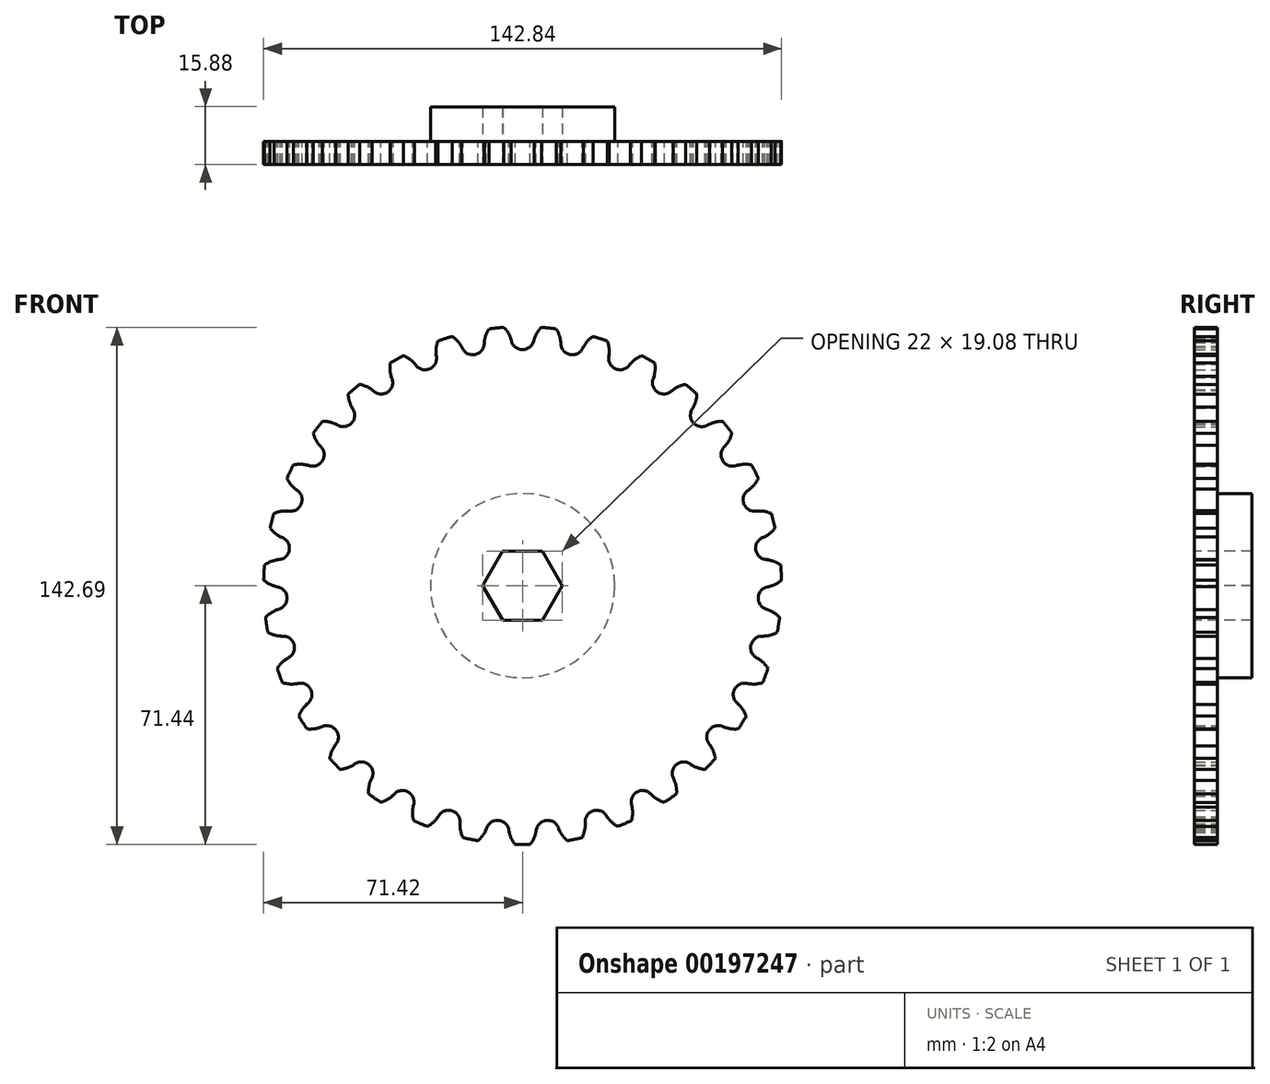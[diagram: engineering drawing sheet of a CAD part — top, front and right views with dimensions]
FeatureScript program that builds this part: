
annotation { "Feature Type Name" : "Feature", "Feature Type Description" : "" }
export const myFeature = defineFeature(function(context is Context, id is Id, definition is map)
    precondition{}
    {
        {
            var Q0;
            Q0=qCreatedBy(makeId("Front.planeOp"),FACE);
            var sketch = newSketch(context, id + "F0", { "sketchPlane" : qUnion([Q0])});
            skCircle(sketch, "E0", {"center": v(0, 0) * mm, "radius": 71.44 * mm});
            skSolve(sketch);
        }
        {
            var Q0;
            Q0 = qSketchRegion(id + "F0", true);
            extrude(context, id + "F1", {"entities" : qUnion([Q0]), "depth" : 6.35 * mm});
        }
        {
            var Q0;
            Q0=qCreatedBy(makeId("Front.planeOp"),FACE);
            var sketch = newSketch(context, id + "F2", { "sketchPlane" : qUnion([Q0])});
            skArc(sketch, "E1", {"start": v(-3.17, 68.11) * mm, "mid": v(0, 65.09) * mm, "end": v(3.17, 68.11) * mm});
            skLineSegment(sketch, "E2", {"start": v(3.17, 68.11) * mm, "end": v(3.33, 71.44) * mm});
            skLineSegment(sketch, "E3", {"start": v(-3.17, 68.11) * mm, "end": v(-3.32, 71.36) * mm});
            skPoint(sketch, "E4.start.orphan", {"position": v(0, 0) * mm});
            skArc(sketch, "E5.1.0", {"start": v(-16.82, 66.08) * mm, "mid": v(-13.1, 63.76) * mm, "end": v(-10.6, 67.36) * mm});
            skLineSegment(sketch, "E5.1.1", {"start": v(-10.6, 67.36) * mm, "end": v(-11.12, 70.64) * mm});
            skLineSegment(sketch, "E5.1.2", {"start": v(-16.82, 66.08) * mm, "end": v(-17.62, 69.23) * mm});
            skArc(sketch, "E5.2.0", {"start": v(-29.78, 61.34) * mm, "mid": v(-25.67, 59.81) * mm, "end": v(-23.95, 63.85) * mm});
            skLineSegment(sketch, "E5.2.1", {"start": v(-23.95, 63.85) * mm, "end": v(-25.12, 66.96) * mm});
            skLineSegment(sketch, "E5.2.2", {"start": v(-29.78, 61.34) * mm, "end": v(-31.2, 64.27) * mm});
            skArc(sketch, "E5.3.0", {"start": v(-41.51, 54.1) * mm, "mid": v(-37.18, 53.42) * mm, "end": v(-36.3, 57.72) * mm});
            skLineSegment(sketch, "E5.3.1", {"start": v(-36.3, 57.72) * mm, "end": v(-38.08, 60.53) * mm});
            skLineSegment(sketch, "E5.3.2", {"start": v(-41.51, 54.1) * mm, "end": v(-43.5, 56.67) * mm});
            skArc(sketch, "E5.4.0", {"start": v(-51.55, 44.63) * mm, "mid": v(-47.17, 44.84) * mm, "end": v(-47.18, 49.23) * mm});
            skLineSegment(sketch, "E5.4.1", {"start": v(-47.18, 49.23) * mm, "end": v(-49.49, 51.63) * mm});
            skLineSegment(sketch, "E5.4.2", {"start": v(-51.55, 44.63) * mm, "end": v(-54.01, 46.76) * mm});
            skArc(sketch, "E5.5.0", {"start": v(-59.48, 33.34) * mm, "mid": v(-55.24, 34.43) * mm, "end": v(-56.13, 38.72) * mm});
            skLineSegment(sketch, "E5.5.1", {"start": v(-56.13, 38.72) * mm, "end": v(-58.87, 40.61) * mm});
            skLineSegment(sketch, "E5.5.2", {"start": v(-59.48, 33.34) * mm, "end": v(-62.32, 34.93) * mm});
            skArc(sketch, "E5.6.0", {"start": v(-64.98, 20.68) * mm, "mid": v(-61.04, 22.6) * mm, "end": v(-62.77, 26.63) * mm});
            skLineSegment(sketch, "E5.6.1", {"start": v(-62.77, 26.63) * mm, "end": v(-65.84, 27.93) * mm});
            skLineSegment(sketch, "E5.6.2", {"start": v(-64.98, 20.68) * mm, "end": v(-68.07, 21.67) * mm});
            skArc(sketch, "E5.7.0", {"start": v(-67.8, 7.18) * mm, "mid": v(-64.34, 9.86) * mm, "end": v(-66.85, 13.45) * mm});
            skLineSegment(sketch, "E5.7.1", {"start": v(-66.85, 13.45) * mm, "end": v(-70.11, 14.1) * mm});
            skLineSegment(sketch, "E5.7.2", {"start": v(-67.8, 7.18) * mm, "end": v(-71.04, 7.52) * mm});
            skArc(sketch, "E5.8.0", {"start": v(-67.87, -6.62) * mm, "mid": v(-65, -3.3) * mm, "end": v(-68.19, -0.28) * mm});
            skLineSegment(sketch, "E5.8.1", {"start": v(-68.19, -0.28) * mm, "end": v(-71.51, -0.3) * mm});
            skLineSegment(sketch, "E5.8.2", {"start": v(-67.87, -6.62) * mm, "end": v(-71.1, -6.93) * mm});
            skArc(sketch, "E5.9.0", {"start": v(-65.15, -20.14) * mm, "mid": v(-63, -16.31) * mm, "end": v(-66.74, -14) * mm});
            skLineSegment(sketch, "E5.9.1", {"start": v(-66.74, -14) * mm, "end": v(-70, -14.69) * mm});
            skLineSegment(sketch, "E5.9.2", {"start": v(-65.15, -20.14) * mm, "end": v(-68.25, -21.1) * mm});
            skArc(sketch, "E5.10.0", {"start": v(-59.76, -32.84) * mm, "mid": v(-58.44, -28.66) * mm, "end": v(-62.55, -27.15) * mm});
            skLineSegment(sketch, "E5.10.1", {"start": v(-62.55, -27.15) * mm, "end": v(-65.6, -28.47) * mm});
            skLineSegment(sketch, "E5.10.2", {"start": v(-59.76, -32.84) * mm, "end": v(-62.6, -34.4) * mm});
            skArc(sketch, "E5.11.0", {"start": v(-51.92, -44.2) * mm, "mid": v(-51.47, -39.84) * mm, "end": v(-55.8, -39.19) * mm});
            skLineSegment(sketch, "E5.11.1", {"start": v(-55.8, -39.19) * mm, "end": v(-58.53, -41.1) * mm});
            skLineSegment(sketch, "E5.11.2", {"start": v(-51.92, -44.2) * mm, "end": v(-54.4, -46.3) * mm});
            skArc(sketch, "E5.12.0", {"start": v(-41.96, -53.75) * mm, "mid": v(-42.4, -49.39) * mm, "end": v(-46.77, -49.62) * mm});
            skLineSegment(sketch, "E5.12.1", {"start": v(-46.77, -49.62) * mm, "end": v(-49.06, -52.04) * mm});
            skLineSegment(sketch, "E5.12.2", {"start": v(-41.96, -53.75) * mm, "end": v(-43.96, -56.3) * mm});
            skArc(sketch, "E6", {"start": v(3.32, 71.36) * mm, "mid": v(0, 71.44) * mm, "end": v(-3.32, 71.36) * mm});
            skArc(sketch, "E7.trimOffspring", {"start": v(17.62, 69.23) * mm, "mid": v(14.38, 69.98) * mm, "end": v(11.11, 70.57) * mm});
            skArc(sketch, "E8.trimOffspring", {"start": v(-11.11, 70.57) * mm, "mid": v(-14.38, 69.98) * mm, "end": v(-17.62, 69.23) * mm});
            skArc(sketch, "E9.trimOffspring", {"start": v(-25.09, 66.89) * mm, "mid": v(-28.17, 65.65) * mm, "end": v(-31.2, 64.27) * mm});
            skArc(sketch, "E10.trimOffspring", {"start": v(-38.04, 60.47) * mm, "mid": v(-40.8, 58.63) * mm, "end": v(-43.5, 56.67) * mm});
            skArc(sketch, "E11.trimOffspring", {"start": v(-49.43, 51.57) * mm, "mid": v(-51.78, 49.22) * mm, "end": v(-54.01, 46.76) * mm});
            skArc(sketch, "E12.trimOffspring", {"start": v(-58.8, 40.57) * mm, "mid": v(-60.63, 37.79) * mm, "end": v(-62.32, 34.93) * mm});
            skArc(sketch, "E13.trimOffspring", {"start": v(-65.76, 27.9) * mm, "mid": v(-67, 24.81) * mm, "end": v(-68.07, 21.67) * mm});
            skArc(sketch, "E14.trimOffspring", {"start": v(-70.03, 14.1) * mm, "mid": v(-70.61, 10.82) * mm, "end": v(-71.04, 7.52) * mm});
            skArc(sketch, "E15.trimOffspring", {"start": v(-71.44, -0.3) * mm, "mid": v(-71.35, -3.62) * mm, "end": v(-71.1, -6.93) * mm});
            skArc(sketch, "E16.trimOffspring", {"start": v(-69.92, -14.67) * mm, "mid": v(-69.16, -17.9) * mm, "end": v(-68.25, -21.1) * mm});
            skArc(sketch, "E17.trimOffspring", {"start": v(-65.53, -28.44) * mm, "mid": v(-64.14, -31.46) * mm, "end": v(-62.6, -34.4) * mm});
            skArc(sketch, "E18.trimOffspring", {"start": v(-58.46, -41.05) * mm, "mid": v(-56.5, -43.73) * mm, "end": v(-54.4, -46.3) * mm});
            skArc(sketch, "E19.2.13.0", {"start": v(-30.28, -61.1) * mm, "mid": v(-31.59, -56.9) * mm, "end": v(-35.83, -58.02) * mm});
            skLineSegment(sketch, "E19.4.13.0", {"start": v(-35.83, -58.02) * mm, "end": v(-37.58, -60.85) * mm});
            skLineSegment(sketch, "E19.7.13.0", {"start": v(-30.28, -61.1) * mm, "end": v(-31.73, -64) * mm});
            skArc(sketch, "E19.2.14.0", {"start": v(-17.36, -65.94) * mm, "mid": v(-19.48, -62.1) * mm, "end": v(-23.42, -64.04) * mm});
            skLineSegment(sketch, "E19.4.14.0", {"start": v(-23.42, -64.04) * mm, "end": v(-24.56, -67.17) * mm});
            skLineSegment(sketch, "E19.7.14.0", {"start": v(-17.36, -65.94) * mm, "end": v(-18.2, -69.08) * mm});
            skArc(sketch, "E19.2.15.0", {"start": v(-3.74, -68.09) * mm, "mid": v(-6.58, -64.75) * mm, "end": v(-10.05, -67.44) * mm});
            skLineSegment(sketch, "E19.4.15.0", {"start": v(-10.05, -67.44) * mm, "end": v(-10.54, -70.73) * mm});
            skLineSegment(sketch, "E19.7.15.0", {"start": v(-3.74, -68.09) * mm, "end": v(-3.91, -71.33) * mm});
            skArc(sketch, "E19.2.16.0", {"start": v(10.05, -67.44) * mm, "mid": v(6.58, -64.75) * mm, "end": v(3.74, -68.09) * mm});
            skLineSegment(sketch, "E19.4.16.0", {"start": v(3.74, -68.09) * mm, "end": v(3.92, -71.4) * mm});
            skLineSegment(sketch, "E19.7.16.0", {"start": v(10.05, -67.44) * mm, "end": v(10.53, -70.66) * mm});
            skArc(sketch, "E20.2.17.0", {"start": v(23.42, -64.04) * mm, "mid": v(19.48, -62.1) * mm, "end": v(17.36, -65.94) * mm});
            skLineSegment(sketch, "E20.4.17.0", {"start": v(17.36, -65.94) * mm, "end": v(18.21, -69.16) * mm});
            skLineSegment(sketch, "E20.7.17.0", {"start": v(23.42, -64.04) * mm, "end": v(24.53, -67.1) * mm});
            skArc(sketch, "E20.2.18.0", {"start": v(35.83, -58.02) * mm, "mid": v(31.59, -56.9) * mm, "end": v(30.28, -61.1) * mm});
            skLineSegment(sketch, "E20.4.18.0", {"start": v(30.28, -61.1) * mm, "end": v(31.76, -64.08) * mm});
            skLineSegment(sketch, "E20.7.18.0", {"start": v(35.83, -58.02) * mm, "end": v(37.54, -60.78) * mm});
            skArc(sketch, "E20.2.19.0", {"start": v(46.77, -49.62) * mm, "mid": v(42.4, -49.39) * mm, "end": v(41.96, -53.75) * mm});
            skLineSegment(sketch, "E20.4.19.0", {"start": v(41.96, -53.75) * mm, "end": v(44, -56.37) * mm});
            skLineSegment(sketch, "E20.7.19.0", {"start": v(46.77, -49.62) * mm, "end": v(49, -51.98) * mm});
            skArc(sketch, "E20.2.20.0", {"start": v(55.8, -39.19) * mm, "mid": v(51.47, -39.84) * mm, "end": v(51.92, -44.2) * mm});
            skLineSegment(sketch, "E20.4.20.0", {"start": v(51.92, -44.2) * mm, "end": v(54.46, -46.36) * mm});
            skLineSegment(sketch, "E20.7.20.0", {"start": v(55.8, -39.19) * mm, "end": v(58.46, -41.05) * mm});
            skArc(sketch, "E21.2.21.0", {"start": v(62.55, -27.15) * mm, "mid": v(58.44, -28.66) * mm, "end": v(59.76, -32.84) * mm});
            skLineSegment(sketch, "E21.4.21.0", {"start": v(59.76, -32.84) * mm, "end": v(62.67, -34.45) * mm});
            skLineSegment(sketch, "E21.7.21.0", {"start": v(62.55, -27.15) * mm, "end": v(65.53, -28.44) * mm});
            skArc(sketch, "E21.2.22.0", {"start": v(66.74, -14) * mm, "mid": v(63, -16.31) * mm, "end": v(65.15, -20.14) * mm});
            skLineSegment(sketch, "E21.4.22.0", {"start": v(65.15, -20.14) * mm, "end": v(68.32, -21.13) * mm});
            skLineSegment(sketch, "E21.7.22.0", {"start": v(66.74, -14) * mm, "end": v(69.92, -14.67) * mm});
            skArc(sketch, "E22.2.23.0", {"start": v(68.19, -0.28) * mm, "mid": v(65, -3.3) * mm, "end": v(67.87, -6.62) * mm});
            skLineSegment(sketch, "E22.4.23.0", {"start": v(67.87, -6.62) * mm, "end": v(71.18, -6.94) * mm});
            skLineSegment(sketch, "E22.7.23.0", {"start": v(68.19, -0.28) * mm, "end": v(71.44, -0.3) * mm});
            skArc(sketch, "E22.2.24.0", {"start": v(66.85, 13.45) * mm, "mid": v(64.34, 9.86) * mm, "end": v(67.8, 7.18) * mm});
            skLineSegment(sketch, "E22.4.24.0", {"start": v(67.8, 7.18) * mm, "end": v(71.12, 7.53) * mm});
            skLineSegment(sketch, "E22.7.24.0", {"start": v(66.85, 13.45) * mm, "end": v(70.03, 14.1) * mm});
            skArc(sketch, "E23.2.25.0", {"start": v(62.77, 26.63) * mm, "mid": v(61.04, 22.6) * mm, "end": v(64.98, 20.68) * mm});
            skLineSegment(sketch, "E23.4.25.0", {"start": v(64.98, 20.68) * mm, "end": v(68.15, 21.7) * mm});
            skLineSegment(sketch, "E23.7.25.0", {"start": v(62.77, 26.63) * mm, "end": v(65.76, 27.9) * mm});
            skArc(sketch, "E23.2.26.0", {"start": v(56.13, 38.72) * mm, "mid": v(55.24, 34.43) * mm, "end": v(59.48, 33.34) * mm});
            skLineSegment(sketch, "E23.4.26.0", {"start": v(59.48, 33.34) * mm, "end": v(62.38, 34.97) * mm});
            skLineSegment(sketch, "E23.7.26.0", {"start": v(56.13, 38.72) * mm, "end": v(58.8, 40.57) * mm});
            skArc(sketch, "E23.2.27.0", {"start": v(47.18, 49.23) * mm, "mid": v(47.17, 44.84) * mm, "end": v(51.55, 44.63) * mm});
            skLineSegment(sketch, "E23.4.27.0", {"start": v(51.55, 44.63) * mm, "end": v(54.07, 46.8) * mm});
            skLineSegment(sketch, "E23.7.27.0", {"start": v(47.18, 49.23) * mm, "end": v(49.43, 51.57) * mm});
            skArc(sketch, "E23.2.28.0", {"start": v(36.3, 57.72) * mm, "mid": v(37.18, 53.42) * mm, "end": v(41.51, 54.1) * mm});
            skLineSegment(sketch, "E23.4.28.0", {"start": v(41.51, 54.1) * mm, "end": v(43.54, 56.73) * mm});
            skLineSegment(sketch, "E23.7.28.0", {"start": v(36.3, 57.72) * mm, "end": v(38.04, 60.47) * mm});
            skArc(sketch, "E24.2.29.0", {"start": v(23.95, 63.85) * mm, "mid": v(25.67, 59.81) * mm, "end": v(29.78, 61.34) * mm});
            skLineSegment(sketch, "E24.4.29.0", {"start": v(29.78, 61.34) * mm, "end": v(31.23, 64.34) * mm});
            skLineSegment(sketch, "E24.7.29.0", {"start": v(23.95, 63.85) * mm, "end": v(25.09, 66.89) * mm});
            skArc(sketch, "E24.2.30.0", {"start": v(10.6, 67.36) * mm, "mid": v(13.1, 63.76) * mm, "end": v(16.82, 66.08) * mm});
            skLineSegment(sketch, "E24.4.30.0", {"start": v(16.82, 66.08) * mm, "end": v(17.64, 69.3) * mm});
            skLineSegment(sketch, "E24.7.30.0", {"start": v(10.6, 67.36) * mm, "end": v(11.11, 70.57) * mm});
            skArc(sketch, "E25", {"start": v(3.32, 71.36) * mm, "mid": v(-51.78, 49.22) * mm, "end": v(-71.1, -6.93) * mm});
            skArc(sketch, "E26.trimOffspring", {"start": v(31.2, 64.27) * mm, "mid": v(28.17, 65.65) * mm, "end": v(25.09, 66.89) * mm});
            skArc(sketch, "E27.trimOffspring", {"start": v(43.5, 56.67) * mm, "mid": v(40.8, 58.63) * mm, "end": v(38.04, 60.47) * mm});
            skArc(sketch, "E28.trimOffspring", {"start": v(54.01, 46.76) * mm, "mid": v(51.78, 49.22) * mm, "end": v(49.43, 51.57) * mm});
            skArc(sketch, "E29.trimOffspring", {"start": v(62.32, 34.93) * mm, "mid": v(60.63, 37.79) * mm, "end": v(58.8, 40.57) * mm});
            skArc(sketch, "E30.trimOffspring", {"start": v(68.07, 21.67) * mm, "mid": v(67, 24.81) * mm, "end": v(65.76, 27.9) * mm});
            skArc(sketch, "E31.trimOffspring", {"start": v(71.04, 7.52) * mm, "mid": v(70.61, 10.82) * mm, "end": v(70.03, 14.1) * mm});
            skArc(sketch, "E32.trimOffspring", {"start": v(71.1, -6.93) * mm, "mid": v(71.35, -3.62) * mm, "end": v(71.44, -0.3) * mm});
            skArc(sketch, "E33.trimOffspring", {"start": v(68.25, -21.1) * mm, "mid": v(69.16, -17.9) * mm, "end": v(69.92, -14.67) * mm});
            skArc(sketch, "E34.trimOffspring", {"start": v(62.6, -34.4) * mm, "mid": v(64.14, -31.46) * mm, "end": v(65.53, -28.44) * mm});
            skArc(sketch, "E35.trimOffspring", {"start": v(54.4, -46.3) * mm, "mid": v(56.5, -43.73) * mm, "end": v(58.46, -41.05) * mm});
            skArc(sketch, "E36.trimOffspring", {"start": v(43.96, -56.3) * mm, "mid": v(46.53, -54.2) * mm, "end": v(49, -51.98) * mm});
            skArc(sketch, "E37.trimOffspring", {"start": v(31.73, -64) * mm, "mid": v(34.67, -62.46) * mm, "end": v(37.54, -60.78) * mm});
            skArc(sketch, "E38.trimOffspring", {"start": v(18.2, -69.08) * mm, "mid": v(21.39, -68.16) * mm, "end": v(24.53, -67.1) * mm});
            skArc(sketch, "E39.trimOffspring", {"start": v(3.91, -71.33) * mm, "mid": v(7.23, -71.07) * mm, "end": v(10.53, -70.66) * mm});
            skArc(sketch, "E40.trimOffspring", {"start": v(-10.53, -70.66) * mm, "mid": v(-7.23, -71.07) * mm, "end": v(-3.91, -71.33) * mm});
            skArc(sketch, "E41.trimOffspring", {"start": v(-24.53, -67.1) * mm, "mid": v(-21.39, -68.16) * mm, "end": v(-18.2, -69.08) * mm});
            skArc(sketch, "E42.trimOffspring", {"start": v(-37.54, -60.78) * mm, "mid": v(-34.67, -62.46) * mm, "end": v(-31.73, -64) * mm});
            skArc(sketch, "E43.trimOffspring", {"start": v(-49, -51.98) * mm, "mid": v(-46.53, -54.2) * mm, "end": v(-43.96, -56.3) * mm});
            skArc(sketch, "E44.trimOffspring", {"start": v(-69.92, -14.67) * mm, "mid": v(-67, -24.81) * mm, "end": v(-62.6, -34.4) * mm});
            skSolve(sketch);
        }
        {
            var Q0;
            Q0 = qSketchRegion(id + "F2", true);
            extrude(context, id + "F3", {"entities" : qUnion([Q0]), "operationType" : NewBodyOperationType.REMOVE, "depth" : 6.35 * mm});
        }
        {
            var Q0;
            Q0=qCreatedBy(makeId("Front.planeOp"),FACE);
            var sketch = newSketch(context, id + "F4", { "sketchPlane" : qUnion([Q0])});
            skArc(sketch, "E45", {"start": v(5.17, 71.25) * mm, "mid": v(3.94, 69.65) * mm, "end": v(3.16, 67.79) * mm});
            skArc(sketch, "E46", {"start": v(10.55, 67.04) * mm, "mid": v(10.16, 69.02) * mm, "end": v(9.28, 70.83) * mm});
            skLineSegment(sketch, "E47", {"start": v(10.55, 67.04) * mm, "end": v(11.11, 70.57) * mm});
            skLineSegment(sketch, "E48", {"start": v(3.16, 67.79) * mm, "end": v(3.32, 71.36) * mm});
            skArc(sketch, "E49", {"start": v(11.11, 70.57) * mm, "mid": v(10.2, 70.7) * mm, "end": v(9.28, 70.83) * mm});
            skArc(sketch, "E50.trimOffspring", {"start": v(5.17, 71.25) * mm, "mid": v(4.25, 71.31) * mm, "end": v(3.32, 71.36) * mm});
            skArc(sketch, "E51.1.0", {"start": v(-9.28, 70.83) * mm, "mid": v(-10.2, 70.7) * mm, "end": v(-11.11, 70.57) * mm});
            skArc(sketch, "E51.1.1", {"start": v(-9.28, 70.83) * mm, "mid": v(-10.16, 69.02) * mm, "end": v(-10.55, 67.04) * mm});
            skLineSegment(sketch, "E51.1.2", {"start": v(-3.16, 67.79) * mm, "end": v(-3.32, 71.36) * mm});
            skLineSegment(sketch, "E51.1.3", {"start": v(-10.55, 67.04) * mm, "end": v(-11.11, 70.57) * mm});
            skArc(sketch, "E51.1.4", {"start": v(-3.16, 67.79) * mm, "mid": v(-3.94, 69.65) * mm, "end": v(-5.17, 71.25) * mm});
            skArc(sketch, "E51.1.5", {"start": v(-3.32, 71.36) * mm, "mid": v(-4.25, 71.31) * mm, "end": v(-5.17, 71.25) * mm});
            skArc(sketch, "E51.2.0", {"start": v(-23.35, 67.51) * mm, "mid": v(-24.22, 67.2) * mm, "end": v(-25.09, 66.89) * mm});
            skArc(sketch, "E51.2.1", {"start": v(-23.35, 67.51) * mm, "mid": v(-23.85, 65.56) * mm, "end": v(-23.83, 63.54) * mm});
            skLineSegment(sketch, "E51.2.2", {"start": v(-16.74, 65.76) * mm, "end": v(-17.62, 69.23) * mm});
            skLineSegment(sketch, "E51.2.3", {"start": v(-23.83, 63.54) * mm, "end": v(-25.09, 66.89) * mm});
            skArc(sketch, "E51.2.4", {"start": v(-16.74, 65.76) * mm, "mid": v(-17.88, 67.43) * mm, "end": v(-19.4, 68.75) * mm});
            skArc(sketch, "E51.2.5", {"start": v(-17.62, 69.23) * mm, "mid": v(-18.51, 69) * mm, "end": v(-19.4, 68.75) * mm});
            skArc(sketch, "E51.3.0", {"start": v(-36.46, 61.43) * mm, "mid": v(-37.25, 60.96) * mm, "end": v(-38.04, 60.47) * mm});
            skArc(sketch, "E51.3.1", {"start": v(-36.46, 61.43) * mm, "mid": v(-36.55, 59.42) * mm, "end": v(-36.13, 57.44) * mm});
            skLineSegment(sketch, "E51.3.2", {"start": v(-29.63, 61.05) * mm, "end": v(-31.2, 64.27) * mm});
            skLineSegment(sketch, "E51.3.3", {"start": v(-36.13, 57.44) * mm, "end": v(-38.04, 60.47) * mm});
            skArc(sketch, "E51.3.4", {"start": v(-29.63, 61.05) * mm, "mid": v(-31.09, 62.45) * mm, "end": v(-32.85, 63.44) * mm});
            skArc(sketch, "E51.3.5", {"start": v(-31.2, 64.27) * mm, "mid": v(-32.02, 63.86) * mm, "end": v(-32.85, 63.44) * mm});
            skArc(sketch, "E51.4.0", {"start": v(-48.08, 52.83) * mm, "mid": v(-48.76, 52.2) * mm, "end": v(-49.43, 51.57) * mm});
            skArc(sketch, "E51.4.1", {"start": v(-48.08, 52.83) * mm, "mid": v(-47.77, 50.84) * mm, "end": v(-46.96, 49) * mm});
            skLineSegment(sketch, "E51.4.2", {"start": v(-41.32, 53.83) * mm, "end": v(-43.5, 56.67) * mm});
            skLineSegment(sketch, "E51.4.3", {"start": v(-46.96, 49) * mm, "end": v(-49.43, 51.57) * mm});
            skArc(sketch, "E51.4.4", {"start": v(-41.32, 53.83) * mm, "mid": v(-43.02, 54.91) * mm, "end": v(-44.94, 55.53) * mm});
            skArc(sketch, "E51.4.5", {"start": v(-43.5, 56.67) * mm, "mid": v(-44.22, 56.1) * mm, "end": v(-44.94, 55.53) * mm});
            skArc(sketch, "E51.5.0", {"start": v(-57.73, 42.07) * mm, "mid": v(-58.27, 41.32) * mm, "end": v(-58.8, 40.57) * mm});
            skArc(sketch, "E51.5.1", {"start": v(-57.73, 42.07) * mm, "mid": v(-57.02, 40.19) * mm, "end": v(-55.86, 38.54) * mm});
            skLineSegment(sketch, "E51.5.2", {"start": v(-51.3, 44.42) * mm, "end": v(-54.01, 46.76) * mm});
            skLineSegment(sketch, "E51.5.3", {"start": v(-55.86, 38.54) * mm, "end": v(-58.8, 40.57) * mm});
            skArc(sketch, "E51.5.4", {"start": v(-51.3, 44.42) * mm, "mid": v(-53.2, 45.13) * mm, "end": v(-55.2, 45.34) * mm});
            skArc(sketch, "E51.5.5", {"start": v(-54.01, 46.76) * mm, "mid": v(-54.61, 46.05) * mm, "end": v(-55.2, 45.34) * mm});
            skArc(sketch, "E51.6.0", {"start": v(-65.02, 29.6) * mm, "mid": v(-65.4, 28.75) * mm, "end": v(-65.76, 27.9) * mm});
            skArc(sketch, "E51.6.1", {"start": v(-65.02, 29.6) * mm, "mid": v(-63.94, 27.88) * mm, "end": v(-62.47, 26.5) * mm});
            skLineSegment(sketch, "E51.6.2", {"start": v(-59.2, 33.18) * mm, "end": v(-62.32, 34.93) * mm});
            skLineSegment(sketch, "E51.6.3", {"start": v(-62.47, 26.5) * mm, "end": v(-65.76, 27.9) * mm});
            skArc(sketch, "E51.6.4", {"start": v(-59.2, 33.18) * mm, "mid": v(-61.2, 33.5) * mm, "end": v(-63.2, 33.3) * mm});
            skArc(sketch, "E51.6.5", {"start": v(-62.32, 34.93) * mm, "mid": v(-62.76, 34.12) * mm, "end": v(-63.2, 33.3) * mm});
            skArc(sketch, "E51.7.0", {"start": v(-69.65, 15.9) * mm, "mid": v(-69.85, 15) * mm, "end": v(-70.03, 14.1) * mm});
            skArc(sketch, "E51.7.1", {"start": v(-69.65, 15.9) * mm, "mid": v(-68.25, 14.44) * mm, "end": v(-66.53, 13.38) * mm});
            skLineSegment(sketch, "E51.7.2", {"start": v(-64.66, 20.58) * mm, "end": v(-68.07, 21.67) * mm});
            skLineSegment(sketch, "E51.7.3", {"start": v(-66.53, 13.38) * mm, "end": v(-70.03, 14.1) * mm});
            skArc(sketch, "E51.7.4", {"start": v(-64.66, 20.58) * mm, "mid": v(-66.68, 20.5) * mm, "end": v(-68.61, 19.9) * mm});
            skArc(sketch, "E51.7.5", {"start": v(-68.07, 21.67) * mm, "mid": v(-68.35, 20.79) * mm, "end": v(-68.61, 19.9) * mm});
            skArc(sketch, "E51.8.0", {"start": v(-71.42, 1.55) * mm, "mid": v(-71.43, 0.63) * mm, "end": v(-71.44, -0.3) * mm});
            skArc(sketch, "E51.8.1", {"start": v(-71.42, 1.55) * mm, "mid": v(-69.76, 0.4) * mm, "end": v(-67.86, -0.28) * mm});
            skLineSegment(sketch, "E51.8.2", {"start": v(-67.48, 7.14) * mm, "end": v(-71.04, 7.52) * mm});
            skLineSegment(sketch, "E51.8.3", {"start": v(-67.86, -0.28) * mm, "end": v(-71.44, -0.3) * mm});
            skArc(sketch, "E51.8.4", {"start": v(-67.48, 7.14) * mm, "mid": v(-69.44, 6.65) * mm, "end": v(-71.21, 5.68) * mm});
            skArc(sketch, "E51.8.5", {"start": v(-71.04, 7.52) * mm, "mid": v(-71.13, 6.6) * mm, "end": v(-71.21, 5.68) * mm});
            skArc(sketch, "E51.9.0", {"start": v(-70.27, -12.86) * mm, "mid": v(-70.1, -13.76) * mm, "end": v(-69.92, -14.67) * mm});
            skArc(sketch, "E51.9.1", {"start": v(-70.27, -12.86) * mm, "mid": v(-68.41, -13.64) * mm, "end": v(-66.41, -13.94) * mm});
            skLineSegment(sketch, "E51.9.2", {"start": v(-67.54, -6.59) * mm, "end": v(-71.1, -6.93) * mm});
            skLineSegment(sketch, "E51.9.3", {"start": v(-66.41, -13.94) * mm, "end": v(-69.92, -14.67) * mm});
            skArc(sketch, "E51.9.4", {"start": v(-67.54, -6.59) * mm, "mid": v(-69.36, -7.46) * mm, "end": v(-70.9, -8.77) * mm});
            skArc(sketch, "E51.9.5", {"start": v(-71.1, -6.93) * mm, "mid": v(-71, -7.85) * mm, "end": v(-70.9, -8.77) * mm});
            skArc(sketch, "E51.10.0", {"start": v(-66.24, -26.74) * mm, "mid": v(-65.9, -27.6) * mm, "end": v(-65.53, -28.44) * mm});
            skArc(sketch, "E51.10.1", {"start": v(-66.24, -26.74) * mm, "mid": v(-64.27, -27.13) * mm, "end": v(-62.25, -27.02) * mm});
            skLineSegment(sketch, "E51.10.2", {"start": v(-64.83, -20.05) * mm, "end": v(-68.25, -21.1) * mm});
            skLineSegment(sketch, "E51.10.3", {"start": v(-62.25, -27.02) * mm, "end": v(-65.53, -28.44) * mm});
            skArc(sketch, "E51.10.4", {"start": v(-64.83, -20.05) * mm, "mid": v(-66.44, -21.27) * mm, "end": v(-67.68, -22.86) * mm});
            skArc(sketch, "E51.10.5", {"start": v(-68.25, -21.1) * mm, "mid": v(-67.97, -21.98) * mm, "end": v(-67.68, -22.86) * mm});
            skArc(sketch, "E51.11.0", {"start": v(-59.5, -39.53) * mm, "mid": v(-59, -40.3) * mm, "end": v(-58.46, -41.05) * mm});
            skArc(sketch, "E51.11.1", {"start": v(-59.5, -39.53) * mm, "mid": v(-57.49, -39.52) * mm, "end": v(-55.54, -39) * mm});
            skLineSegment(sketch, "E51.11.2", {"start": v(-59.47, -32.69) * mm, "end": v(-62.6, -34.4) * mm});
            skLineSegment(sketch, "E51.11.3", {"start": v(-55.54, -39) * mm, "end": v(-58.46, -41.05) * mm});
            skArc(sketch, "E51.11.4", {"start": v(-59.47, -32.69) * mm, "mid": v(-60.8, -34.21) * mm, "end": v(-61.7, -36.02) * mm});
            skArc(sketch, "E51.11.5", {"start": v(-62.6, -34.4) * mm, "mid": v(-62.15, -35.22) * mm, "end": v(-61.7, -36.02) * mm});
            skArc(sketch, "E51.12.0", {"start": v(-50.33, -50.7) * mm, "mid": v(-49.67, -51.34) * mm, "end": v(-49, -51.98) * mm});
            skArc(sketch, "E51.12.1", {"start": v(-50.33, -50.7) * mm, "mid": v(-48.36, -50.28) * mm, "end": v(-46.55, -49.38) * mm});
            skLineSegment(sketch, "E51.12.2", {"start": v(-51.67, -43.99) * mm, "end": v(-54.4, -46.3) * mm});
            skLineSegment(sketch, "E51.12.3", {"start": v(-46.55, -49.38) * mm, "end": v(-49, -51.98) * mm});
            skArc(sketch, "E51.12.4", {"start": v(-51.67, -43.99) * mm, "mid": v(-52.66, -45.75) * mm, "end": v(-53.18, -47.7) * mm});
            skArc(sketch, "E51.12.5", {"start": v(-54.4, -46.3) * mm, "mid": v(-53.8, -47) * mm, "end": v(-53.18, -47.7) * mm});
            skArc(sketch, "E51.13.0", {"start": v(-39.1, -59.79) * mm, "mid": v(-38.32, -60.3) * mm, "end": v(-37.54, -60.78) * mm});
            skArc(sketch, "E51.13.1", {"start": v(-39.1, -59.79) * mm, "mid": v(-37.25, -58.98) * mm, "end": v(-35.66, -57.74) * mm});
            skLineSegment(sketch, "E51.13.2", {"start": v(-41.76, -53.5) * mm, "end": v(-43.96, -56.3) * mm});
            skLineSegment(sketch, "E51.13.3", {"start": v(-35.66, -57.74) * mm, "end": v(-37.54, -60.78) * mm});
            skArc(sketch, "E51.13.4", {"start": v(-41.76, -53.5) * mm, "mid": v(-42.38, -55.41) * mm, "end": v(-42.49, -57.43) * mm});
            skArc(sketch, "E51.13.5", {"start": v(-43.96, -56.3) * mm, "mid": v(-43.23, -56.87) * mm, "end": v(-42.49, -57.43) * mm});
            skArc(sketch, "E51.14.0", {"start": v(-26.26, -66.44) * mm, "mid": v(-25.4, -66.77) * mm, "end": v(-24.53, -67.1) * mm});
            skArc(sketch, "E51.14.1", {"start": v(-26.26, -66.44) * mm, "mid": v(-24.6, -65.27) * mm, "end": v(-23.3, -63.73) * mm});
            skLineSegment(sketch, "E51.14.2", {"start": v(-30.14, -60.8) * mm, "end": v(-31.73, -64) * mm});
            skLineSegment(sketch, "E51.14.3", {"start": v(-23.3, -63.73) * mm, "end": v(-24.53, -67.1) * mm});
            skArc(sketch, "E51.14.4", {"start": v(-30.14, -60.8) * mm, "mid": v(-30.36, -62.8) * mm, "end": v(-30.06, -64.8) * mm});
            skArc(sketch, "E51.14.5", {"start": v(-31.73, -64) * mm, "mid": v(-30.9, -64.41) * mm, "end": v(-30.06, -64.8) * mm});
            skArc(sketch, "E51.15.0", {"start": v(-12.35, -70.36) * mm, "mid": v(-11.44, -70.52) * mm, "end": v(-10.53, -70.66) * mm});
            skArc(sketch, "E51.15.1", {"start": v(-12.35, -70.36) * mm, "mid": v(-10.97, -68.9) * mm, "end": v(-10, -67.12) * mm});
            skLineSegment(sketch, "E51.15.2", {"start": v(-17.28, -65.62) * mm, "end": v(-18.2, -69.08) * mm});
            skLineSegment(sketch, "E51.15.3", {"start": v(-10, -67.12) * mm, "end": v(-10.53, -70.66) * mm});
            skArc(sketch, "E51.15.4", {"start": v(-17.28, -65.62) * mm, "mid": v(-17.1, -67.63) * mm, "end": v(-16.4, -69.53) * mm});
            skArc(sketch, "E51.15.5", {"start": v(-18.2, -69.08) * mm, "mid": v(-17.3, -69.31) * mm, "end": v(-16.4, -69.53) * mm});
            skArc(sketch, "E51.16.0", {"start": v(2.07, -71.4) * mm, "mid": v(3, -71.37) * mm, "end": v(3.91, -71.33) * mm});
            skArc(sketch, "E51.16.1", {"start": v(2.07, -71.4) * mm, "mid": v(3.13, -69.69) * mm, "end": v(3.72, -67.76) * mm});
            skLineSegment(sketch, "E51.16.2", {"start": v(-3.72, -67.76) * mm, "end": v(-3.91, -71.33) * mm});
            skLineSegment(sketch, "E51.16.3", {"start": v(3.72, -67.76) * mm, "end": v(3.91, -71.33) * mm});
            skArc(sketch, "E51.16.4", {"start": v(-3.72, -67.76) * mm, "mid": v(-3.13, -69.69) * mm, "end": v(-2.07, -71.4) * mm});
            skArc(sketch, "E51.16.5", {"start": v(-3.91, -71.33) * mm, "mid": v(-3, -71.37) * mm, "end": v(-2.07, -71.4) * mm});
            skArc(sketch, "E51.17.0", {"start": v(16.4, -69.53) * mm, "mid": v(17.3, -69.31) * mm, "end": v(18.2, -69.08) * mm});
            skArc(sketch, "E51.17.1", {"start": v(16.4, -69.53) * mm, "mid": v(17.1, -67.63) * mm, "end": v(17.28, -65.62) * mm});
            skLineSegment(sketch, "E51.17.2", {"start": v(10, -67.12) * mm, "end": v(10.53, -70.66) * mm});
            skLineSegment(sketch, "E51.17.3", {"start": v(17.28, -65.62) * mm, "end": v(18.2, -69.08) * mm});
            skArc(sketch, "E51.17.4", {"start": v(10, -67.12) * mm, "mid": v(10.97, -68.9) * mm, "end": v(12.35, -70.36) * mm});
            skArc(sketch, "E51.17.5", {"start": v(10.53, -70.66) * mm, "mid": v(11.44, -70.52) * mm, "end": v(12.35, -70.36) * mm});
            skArc(sketch, "E51.18.0", {"start": v(30.06, -64.8) * mm, "mid": v(30.9, -64.41) * mm, "end": v(31.73, -64) * mm});
            skArc(sketch, "E51.18.1", {"start": v(30.06, -64.8) * mm, "mid": v(30.36, -62.8) * mm, "end": v(30.14, -60.8) * mm});
            skLineSegment(sketch, "E51.18.2", {"start": v(23.3, -63.73) * mm, "end": v(24.53, -67.1) * mm});
            skLineSegment(sketch, "E51.18.3", {"start": v(30.14, -60.8) * mm, "end": v(31.73, -64) * mm});
            skArc(sketch, "E51.18.4", {"start": v(23.3, -63.73) * mm, "mid": v(24.6, -65.27) * mm, "end": v(26.26, -66.44) * mm});
            skArc(sketch, "E51.18.5", {"start": v(24.53, -67.1) * mm, "mid": v(25.4, -66.77) * mm, "end": v(26.26, -66.44) * mm});
            skArc(sketch, "E51.19.0", {"start": v(42.49, -57.43) * mm, "mid": v(43.23, -56.87) * mm, "end": v(43.96, -56.3) * mm});
            skArc(sketch, "E51.19.1", {"start": v(42.49, -57.43) * mm, "mid": v(42.38, -55.41) * mm, "end": v(41.76, -53.5) * mm});
            skLineSegment(sketch, "E51.19.2", {"start": v(35.66, -57.74) * mm, "end": v(37.54, -60.78) * mm});
            skLineSegment(sketch, "E51.19.3", {"start": v(41.76, -53.5) * mm, "end": v(43.96, -56.3) * mm});
            skArc(sketch, "E51.19.4", {"start": v(35.66, -57.74) * mm, "mid": v(37.25, -58.98) * mm, "end": v(39.1, -59.79) * mm});
            skArc(sketch, "E51.19.5", {"start": v(37.54, -60.78) * mm, "mid": v(38.32, -60.3) * mm, "end": v(39.1, -59.79) * mm});
            skArc(sketch, "E51.20.0", {"start": v(53.18, -47.7) * mm, "mid": v(53.8, -47) * mm, "end": v(54.4, -46.3) * mm});
            skArc(sketch, "E51.20.1", {"start": v(53.18, -47.7) * mm, "mid": v(52.66, -45.75) * mm, "end": v(51.67, -43.99) * mm});
            skLineSegment(sketch, "E51.20.2", {"start": v(46.55, -49.38) * mm, "end": v(49, -51.98) * mm});
            skLineSegment(sketch, "E51.20.3", {"start": v(51.67, -43.99) * mm, "end": v(54.4, -46.3) * mm});
            skArc(sketch, "E51.20.4", {"start": v(46.55, -49.38) * mm, "mid": v(48.36, -50.28) * mm, "end": v(50.33, -50.7) * mm});
            skArc(sketch, "E51.20.5", {"start": v(49, -51.98) * mm, "mid": v(49.67, -51.34) * mm, "end": v(50.33, -50.7) * mm});
            skArc(sketch, "E51.21.0", {"start": v(61.7, -36.02) * mm, "mid": v(62.15, -35.22) * mm, "end": v(62.6, -34.4) * mm});
            skArc(sketch, "E51.21.1", {"start": v(61.7, -36.02) * mm, "mid": v(60.8, -34.21) * mm, "end": v(59.47, -32.69) * mm});
            skLineSegment(sketch, "E51.21.2", {"start": v(55.54, -39) * mm, "end": v(58.46, -41.05) * mm});
            skLineSegment(sketch, "E51.21.3", {"start": v(59.47, -32.69) * mm, "end": v(62.6, -34.4) * mm});
            skArc(sketch, "E51.21.4", {"start": v(55.54, -39) * mm, "mid": v(57.49, -39.52) * mm, "end": v(59.5, -39.53) * mm});
            skArc(sketch, "E51.21.5", {"start": v(58.46, -41.05) * mm, "mid": v(59, -40.3) * mm, "end": v(59.5, -39.53) * mm});
            skArc(sketch, "E51.22.0", {"start": v(67.68, -22.86) * mm, "mid": v(67.97, -21.98) * mm, "end": v(68.25, -21.1) * mm});
            skArc(sketch, "E51.22.1", {"start": v(67.68, -22.86) * mm, "mid": v(66.44, -21.27) * mm, "end": v(64.83, -20.05) * mm});
            skLineSegment(sketch, "E51.22.2", {"start": v(62.25, -27.02) * mm, "end": v(65.53, -28.44) * mm});
            skLineSegment(sketch, "E51.22.3", {"start": v(64.83, -20.05) * mm, "end": v(68.25, -21.1) * mm});
            skArc(sketch, "E51.22.4", {"start": v(62.25, -27.02) * mm, "mid": v(64.27, -27.13) * mm, "end": v(66.24, -26.74) * mm});
            skArc(sketch, "E51.22.5", {"start": v(65.53, -28.44) * mm, "mid": v(65.9, -27.6) * mm, "end": v(66.24, -26.74) * mm});
            skArc(sketch, "E51.23.0", {"start": v(70.9, -8.77) * mm, "mid": v(71, -7.85) * mm, "end": v(71.1, -6.93) * mm});
            skArc(sketch, "E51.23.1", {"start": v(70.9, -8.77) * mm, "mid": v(69.36, -7.46) * mm, "end": v(67.54, -6.59) * mm});
            skLineSegment(sketch, "E51.23.2", {"start": v(66.41, -13.94) * mm, "end": v(69.92, -14.67) * mm});
            skLineSegment(sketch, "E51.23.3", {"start": v(67.54, -6.59) * mm, "end": v(71.1, -6.93) * mm});
            skArc(sketch, "E51.23.4", {"start": v(66.41, -13.94) * mm, "mid": v(68.41, -13.64) * mm, "end": v(70.27, -12.86) * mm});
            skArc(sketch, "E51.23.5", {"start": v(69.92, -14.67) * mm, "mid": v(70.1, -13.76) * mm, "end": v(70.27, -12.86) * mm});
            skArc(sketch, "E51.24.0", {"start": v(71.21, 5.68) * mm, "mid": v(71.13, 6.6) * mm, "end": v(71.04, 7.52) * mm});
            skArc(sketch, "E51.24.1", {"start": v(71.21, 5.68) * mm, "mid": v(69.44, 6.65) * mm, "end": v(67.48, 7.14) * mm});
            skLineSegment(sketch, "E51.24.2", {"start": v(67.86, -0.28) * mm, "end": v(71.44, -0.3) * mm});
            skLineSegment(sketch, "E51.24.3", {"start": v(67.48, 7.14) * mm, "end": v(71.04, 7.52) * mm});
            skArc(sketch, "E51.24.4", {"start": v(67.86, -0.28) * mm, "mid": v(69.76, 0.4) * mm, "end": v(71.42, 1.55) * mm});
            skArc(sketch, "E51.24.5", {"start": v(71.44, -0.3) * mm, "mid": v(71.43, 0.63) * mm, "end": v(71.42, 1.55) * mm});
            skArc(sketch, "E51.25.0", {"start": v(68.61, 19.9) * mm, "mid": v(68.35, 20.79) * mm, "end": v(68.07, 21.67) * mm});
            skArc(sketch, "E51.25.1", {"start": v(68.61, 19.9) * mm, "mid": v(66.68, 20.5) * mm, "end": v(64.66, 20.58) * mm});
            skLineSegment(sketch, "E51.25.2", {"start": v(66.53, 13.38) * mm, "end": v(70.03, 14.1) * mm});
            skLineSegment(sketch, "E51.25.3", {"start": v(64.66, 20.58) * mm, "end": v(68.07, 21.67) * mm});
            skArc(sketch, "E51.25.4", {"start": v(66.53, 13.38) * mm, "mid": v(68.25, 14.44) * mm, "end": v(69.65, 15.9) * mm});
            skArc(sketch, "E51.25.5", {"start": v(70.03, 14.1) * mm, "mid": v(69.85, 15) * mm, "end": v(69.65, 15.9) * mm});
            skArc(sketch, "E51.26.0", {"start": v(63.2, 33.3) * mm, "mid": v(62.76, 34.12) * mm, "end": v(62.32, 34.93) * mm});
            skArc(sketch, "E51.26.1", {"start": v(63.2, 33.3) * mm, "mid": v(61.2, 33.5) * mm, "end": v(59.2, 33.18) * mm});
            skLineSegment(sketch, "E51.26.2", {"start": v(62.47, 26.5) * mm, "end": v(65.76, 27.9) * mm});
            skLineSegment(sketch, "E51.26.3", {"start": v(59.2, 33.18) * mm, "end": v(62.32, 34.93) * mm});
            skArc(sketch, "E51.26.4", {"start": v(62.47, 26.5) * mm, "mid": v(63.94, 27.88) * mm, "end": v(65.02, 29.6) * mm});
            skArc(sketch, "E51.26.5", {"start": v(65.76, 27.9) * mm, "mid": v(65.4, 28.75) * mm, "end": v(65.02, 29.6) * mm});
            skArc(sketch, "E51.27.0", {"start": v(55.2, 45.34) * mm, "mid": v(54.61, 46.05) * mm, "end": v(54.01, 46.76) * mm});
            skArc(sketch, "E51.27.1", {"start": v(55.2, 45.34) * mm, "mid": v(53.2, 45.13) * mm, "end": v(51.3, 44.42) * mm});
            skLineSegment(sketch, "E51.27.2", {"start": v(55.86, 38.54) * mm, "end": v(58.8, 40.57) * mm});
            skLineSegment(sketch, "E51.27.3", {"start": v(51.3, 44.42) * mm, "end": v(54.01, 46.76) * mm});
            skArc(sketch, "E51.27.4", {"start": v(55.86, 38.54) * mm, "mid": v(57.02, 40.19) * mm, "end": v(57.73, 42.07) * mm});
            skArc(sketch, "E51.27.5", {"start": v(58.8, 40.57) * mm, "mid": v(58.27, 41.32) * mm, "end": v(57.73, 42.07) * mm});
            skArc(sketch, "E51.28.0", {"start": v(44.94, 55.53) * mm, "mid": v(44.22, 56.1) * mm, "end": v(43.5, 56.67) * mm});
            skArc(sketch, "E51.28.1", {"start": v(44.94, 55.53) * mm, "mid": v(43.02, 54.91) * mm, "end": v(41.32, 53.83) * mm});
            skLineSegment(sketch, "E51.28.2", {"start": v(46.96, 49) * mm, "end": v(49.43, 51.57) * mm});
            skLineSegment(sketch, "E51.28.3", {"start": v(41.32, 53.83) * mm, "end": v(43.5, 56.67) * mm});
            skArc(sketch, "E51.28.4", {"start": v(46.96, 49) * mm, "mid": v(47.77, 50.84) * mm, "end": v(48.08, 52.83) * mm});
            skArc(sketch, "E51.28.5", {"start": v(49.43, 51.57) * mm, "mid": v(48.76, 52.2) * mm, "end": v(48.08, 52.83) * mm});
            skArc(sketch, "E51.29.0", {"start": v(32.85, 63.44) * mm, "mid": v(32.02, 63.86) * mm, "end": v(31.2, 64.27) * mm});
            skArc(sketch, "E51.29.1", {"start": v(32.85, 63.44) * mm, "mid": v(31.09, 62.45) * mm, "end": v(29.63, 61.05) * mm});
            skLineSegment(sketch, "E51.29.2", {"start": v(36.13, 57.44) * mm, "end": v(38.04, 60.47) * mm});
            skLineSegment(sketch, "E51.29.3", {"start": v(29.63, 61.05) * mm, "end": v(31.2, 64.27) * mm});
            skArc(sketch, "E51.29.4", {"start": v(36.13, 57.44) * mm, "mid": v(36.55, 59.42) * mm, "end": v(36.46, 61.43) * mm});
            skArc(sketch, "E51.29.5", {"start": v(38.04, 60.47) * mm, "mid": v(37.25, 60.96) * mm, "end": v(36.46, 61.43) * mm});
            skArc(sketch, "E51.30.0", {"start": v(19.4, 68.75) * mm, "mid": v(18.51, 69) * mm, "end": v(17.62, 69.23) * mm});
            skArc(sketch, "E51.30.1", {"start": v(19.4, 68.75) * mm, "mid": v(17.88, 67.43) * mm, "end": v(16.74, 65.76) * mm});
            skLineSegment(sketch, "E51.30.2", {"start": v(23.83, 63.54) * mm, "end": v(25.09, 66.89) * mm});
            skLineSegment(sketch, "E51.30.3", {"start": v(16.74, 65.76) * mm, "end": v(17.62, 69.23) * mm});
            skArc(sketch, "E51.30.4", {"start": v(23.83, 63.54) * mm, "mid": v(23.85, 65.56) * mm, "end": v(23.35, 67.51) * mm});
            skArc(sketch, "E51.30.5", {"start": v(25.09, 66.89) * mm, "mid": v(24.22, 67.2) * mm, "end": v(23.35, 67.51) * mm});
            skSolve(sketch);
        }
        {
            var Q0;
            Q0 = qSketchRegion(id + "F4", true);
            extrude(context, id + "F5", {"entities" : qUnion([Q0]), "operationType" : NewBodyOperationType.REMOVE, "depth" : 6.35 * mm});
        }
        {
            var Q0;
            Q0=qCreatedBy(makeId("Front.planeOp"),FACE);
            var sketch = newSketch(context, id + "F6", { "sketchPlane" : qUnion([Q0])});
            skCircle(sketch, "E52", {"center": v(0, 0) * mm, "radius": 25.4 * mm});
            skSolve(sketch);
        }
        {
            var Q0;
            Q0 = qSketchRegion(id + "F6", true);
            extrude(context, id + "F7", {"entities" : qUnion([Q0]), "operationType" : NewBodyOperationType.ADD, "oppositeDirection" : true, "depth" : 9.52 * mm});
        }
        {
            var Q0;
            Q0=qCreatedBy(makeId("Front.planeOp"),FACE);
            var sketch = newSketch(context, id + "F8", { "sketchPlane" : qUnion([Q0])});
            skCircle(sketch, "E53.cCircle", {"center": v(0, 0) * mm, "radius": 9.53 * mm, "construction": true});
            skLineSegment(sketch, "E53.0", {"start": v(-5.48, -9.54) * mm, "end": v(-11, -0.03) * mm});
            skLineSegment(sketch, "E53.1", {"start": v(-11, -0.03) * mm, "end": v(-5.52, 9.51) * mm});
            skLineSegment(sketch, "E53.2", {"start": v(-5.52, 9.51) * mm, "end": v(5.48, 9.54) * mm});
            skLineSegment(sketch, "E53.3", {"start": v(5.48, 9.54) * mm, "end": v(11, 0.03) * mm});
            skLineSegment(sketch, "E53.4", {"start": v(11, 0.03) * mm, "end": v(5.52, -9.51) * mm});
            skLineSegment(sketch, "E53.5", {"start": v(5.52, -9.51) * mm, "end": v(-5.48, -9.54) * mm});
            skPoint(sketch, "E53.0.midPoint", {"position": v(-8.24, -4.78) * mm});
            skSolve(sketch);
        }
        {
            var Q0;
            Q0 = qSketchRegion(id + "F8", true);
            extrude(context, id + "F9", {"entities" : qUnion([Q0]), "operationType" : NewBodyOperationType.REMOVE, "oppositeDirection" : true, "depth" : 9.52 * mm, "hasSecondDirection" : true, "secondDirectionOppositeDirection" : false, "secondDirectionDepth" : 9.52 * mm});
        }
    });
